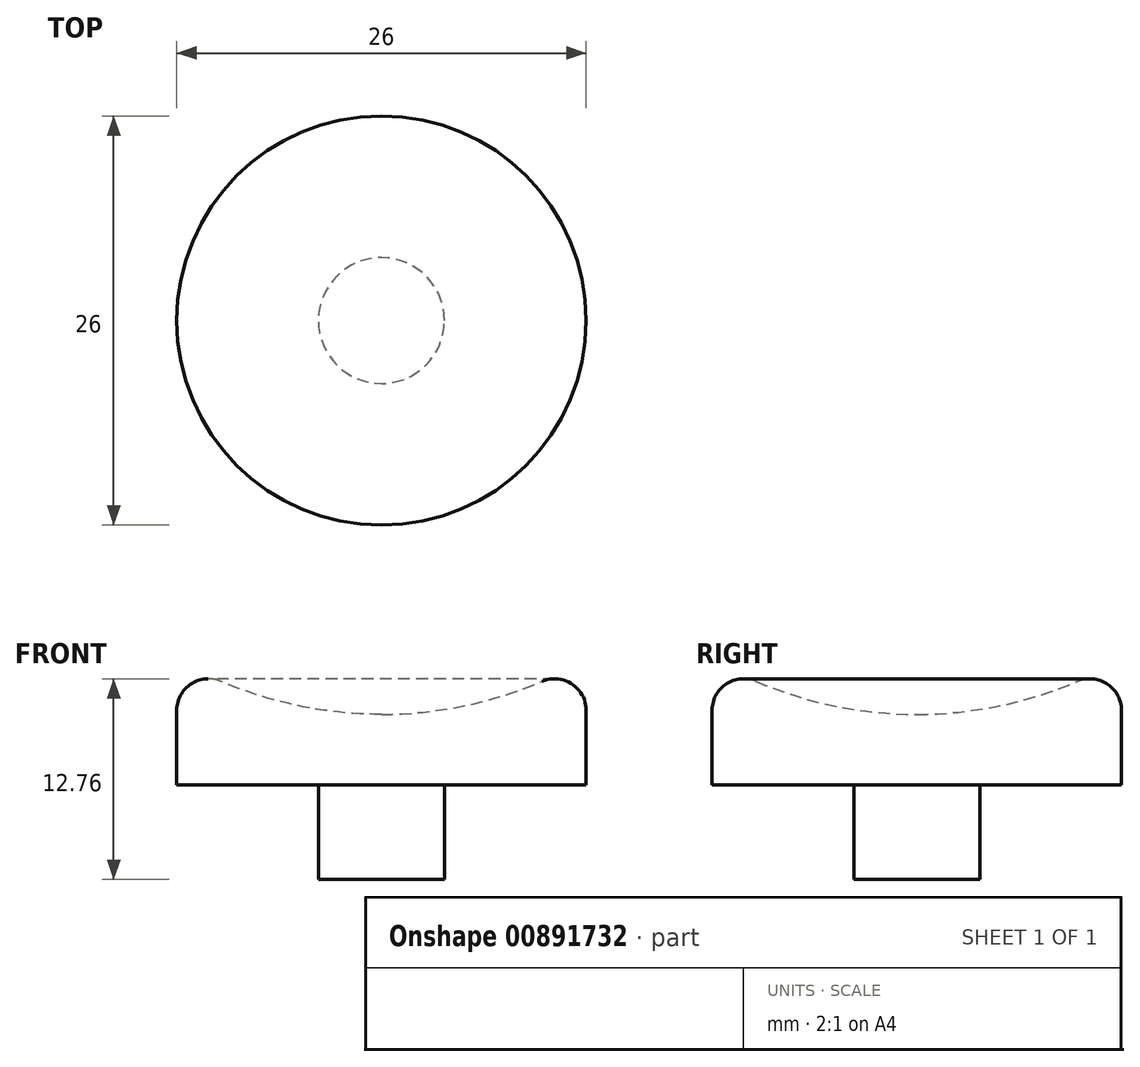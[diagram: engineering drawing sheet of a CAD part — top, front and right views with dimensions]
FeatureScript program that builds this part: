
annotation { "Feature Type Name" : "Feature", "Feature Type Description" : "" }
export const myFeature = defineFeature(function(context is Context, id is Id, definition is map)
    precondition{}
    {
        {
            var Q0;
            Q0=qCreatedBy(makeId("Front.planeOp"),FACE);
            var sketch = newSketch(context, id + "F0", { "sketchPlane" : qUnion([Q0])});
            skLineSegment(sketch, "E0", {"start": v(0, 128.24) * mm, "end": v(0, -112.08) * mm, "construction": true});
            skLineSegment(sketch, "E1", {"start": v(0, 0) * mm, "end": v(4, 0) * mm});
            skLineSegment(sketch, "E2", {"start": v(4, 0) * mm, "end": v(4, 6) * mm});
            skLineSegment(sketch, "E3", {"start": v(4, 6) * mm, "end": v(13, 6) * mm});
            skLineSegment(sketch, "E4", {"start": v(13, 6) * mm, "end": v(13, 14) * mm});
            skArc(sketch, "E5", {"start": v(0, 10.5) * mm, "mid": v(6.73, 11.39) * mm, "end": v(13, 14) * mm});
            skLineSegment(sketch, "E6", {"start": v(0, 0) * mm, "end": v(0, 10.5) * mm});
            skLineSegment(sketch, "E7.MirrorCS", {"start": v(-13, 6) * mm, "end": v(-13, 14) * mm});
            skLineSegment(sketch, "E8.MirrorCS", {"start": v(-4, 0) * mm, "end": v(-4, 6) * mm});
            skLineSegment(sketch, "E9.MirrorCS", {"start": v(-4, 6) * mm, "end": v(-13, 6) * mm});
            skLineSegment(sketch, "E10.MirrorCS", {"start": v(0, 0) * mm, "end": v(-4, 0) * mm});
            skArc(sketch, "E11.MirrorCS", {"start": v(0, 10.5) * mm, "mid": v(-6.73, 11.39) * mm, "end": v(-13, 14) * mm});
            skSolve(sketch);
        }
        {
            var Q0;
            Q0=sQuery(id+"F0.wireOp",EDGE,"E5");
            var Q1;
            Q1=sQuery(id+"F0.wireOp",EDGE,"E4");
            var Q2;
            Q2=sQuery(id+"F0.wireOp",EDGE,"E3");
            var Q3;
            Q3=sQuery(id+"F0.wireOp",EDGE,"E2");
            var Q4;
            Q4=sQuery(id+"F0.wireOp",EDGE,"E6");
            revolve(context, id + "F1", {"bodyType" : ToolBodyType.SURFACE, "surfaceOperationType" : NewSurfaceOperationType.NEW, "surfaceEntities" : qUnion([Q0, Q1, Q2, Q3]), "axis" : qUnion([Q4]), "revolveType" : RevolveType.FULL});
        }
        {
            var Q0;
            Q0=makeQuery(id+"F1.opRevolve","SWEPT_EDGE",EDGE,{"disambiguationData":[OSD([sQuery(id+"F0.wireOp",VERTEX,"E4.end")])]});
            fillet(context, id + "F2", {"entities" : qUnion([Q0]), "radius" : 2 * mm, "tangentPropagation" : true, "allowEdgeOverflow" : false});
        }
    });
